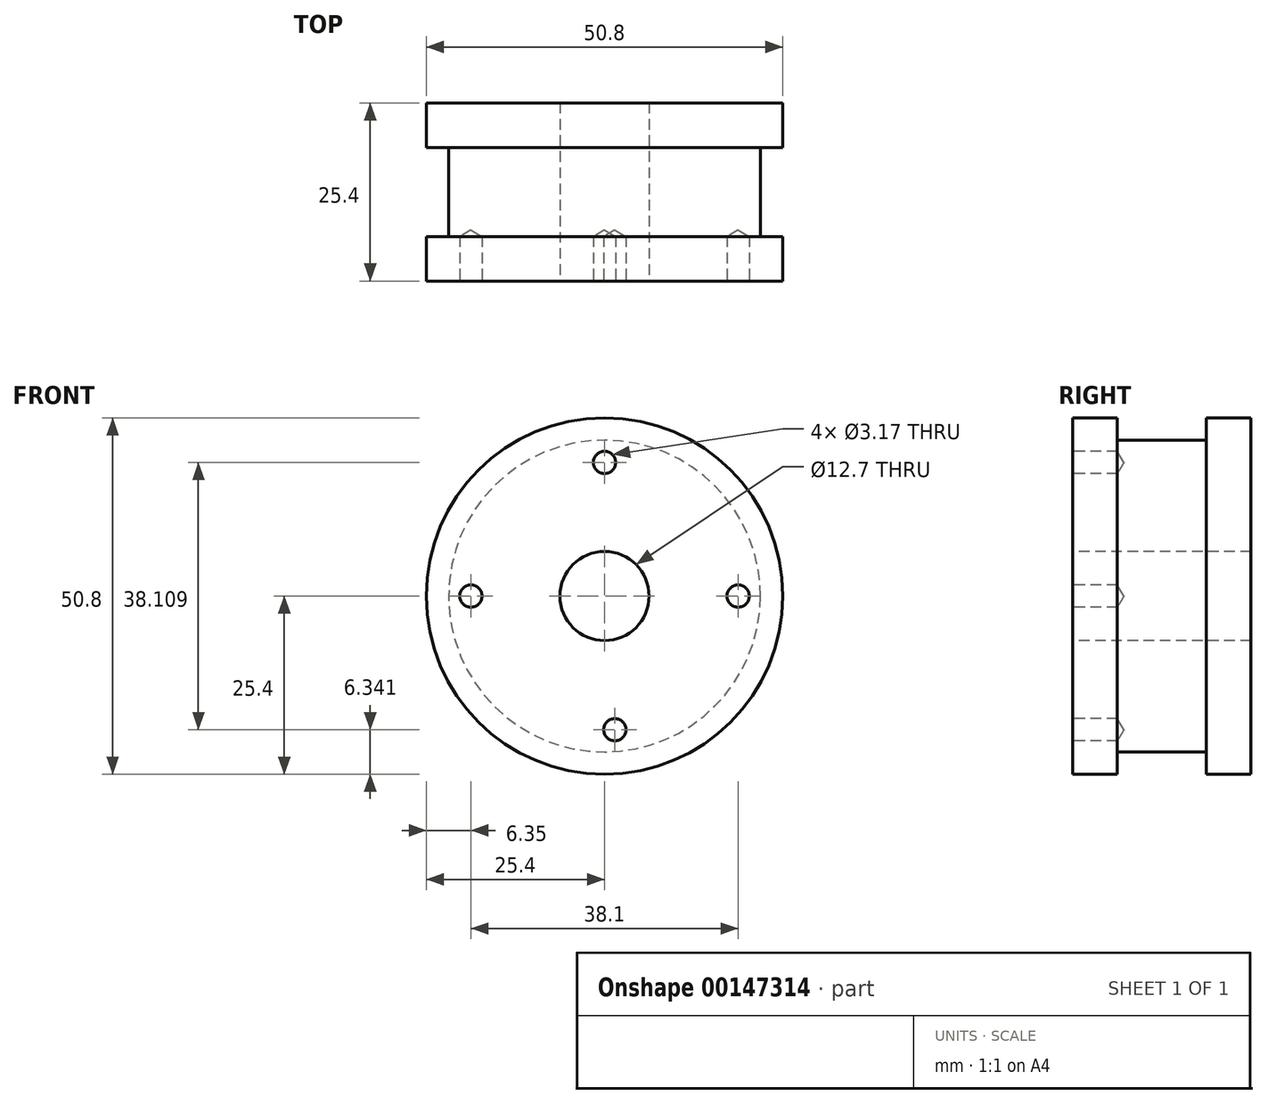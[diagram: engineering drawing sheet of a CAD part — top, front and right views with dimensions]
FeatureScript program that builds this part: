
annotation { "Feature Type Name" : "Feature", "Feature Type Description" : "" }
export const myFeature = defineFeature(function(context is Context, id is Id, definition is map)
    precondition{}
    {
        {
            var Q0;
            Q0=qCreatedBy(makeId("Front.planeOp"),FACE);
            var sketch = newSketch(context, id + "F0", { "sketchPlane" : qUnion([Q0])});
            skCircle(sketch, "E0", {"center": v(0, 0) * mm, "radius": 25.4 * mm});
            skSolve(sketch);
        }
        {
            var Q0;
            Q0 = qSketchRegion(id + "F0", true);
            extrude(context, id + "F1", {"entities" : qUnion([Q0]), "depth" : 6.35 * mm});
        }
        {
            var Q0;
            Q0=makeQuery(id+"F1.opExtrude","CAP_FACE",FACE,{"disambiguationData":[OSD([sQuery(id+"F0.wireOp",EDGE,"E0")])],"isStart":false});
            var sketch = newSketch(context, id + "F2", { "sketchPlane" : qUnion([Q0])});
            skCircle(sketch, "E1", {"center": v(0, 0) * mm, "radius": 22.23 * mm});
            skSolve(sketch);
        }
        {
            var Q0;
            Q0 = qSketchRegion(id + "F2", true);
            extrude(context, id + "F3", {"entities" : qUnion([Q0]), "operationType" : NewBodyOperationType.ADD, "depth" : 12.7 * mm});
        }
        {
            var Q0;
            Q0=makeQuery(id+"F3.opExtrude","CAP_FACE",FACE,{"disambiguationData":[OSD([sQuery(id+"F2.wireOp",EDGE,"E1")])],"isStart":false});
            var sketch = newSketch(context, id + "F4", { "sketchPlane" : qUnion([Q0])});
            skCircle(sketch, "E2", {"center": v(0, 0) * mm, "radius": 25.4 * mm});
            skSolve(sketch);
        }
        {
            var Q0;
            Q0 = qSketchRegion(id + "F4", true);
            extrude(context, id + "F5", {"entities" : qUnion([Q0]), "operationType" : NewBodyOperationType.ADD, "depth" : 6.35 * mm});
        }
        {
            var Q0;
            Q0=makeQuery(id+"F5.opExtrude","CAP_FACE",FACE,{"disambiguationData":[OSD([sQuery(id+"F4.wireOp",EDGE,"E2")])],"isStart":false});
            var sketch = newSketch(context, id + "F6", { "sketchPlane" : qUnion([Q0])});
            skCircle(sketch, "E3", {"center": v(0, -20.64) * mm, "radius": 1.59 * mm});
            skCircle(sketch, "E4", {"center": v(20.64, 0) * mm, "radius": 1.59 * mm});
            skCircle(sketch, "E5", {"center": v(0, 20.64) * mm, "radius": 1.59 * mm});
            skCircle(sketch, "E6", {"center": v(-20.64, 0) * mm, "radius": 1.59 * mm});
            skCircle(sketch, "E7", {"center": v(0, 0) * mm, "radius": 6.35 * mm});
            skSolve(sketch);
        }
        {
            var Q0;
            Q0 = qSketchRegion(id + "F6", true);
            extrude(context, id + "F7", {"entities" : qUnion([Q0]), "operationType" : NewBodyOperationType.REMOVE, "endBound" : BoundingType.THROUGH_ALL, "depth" : 25.4 * mm});
        }
        {
            var Q0;
            Q0=makeQuery(id+"F5.opExtrude","CAP_FACE",FACE,{"disambiguationData":[OSD([sQuery(id+"F4.wireOp",EDGE,"E2")])],"isStart":false});
            var sketch = newSketch(context, id + "F8", { "sketchPlane" : qUnion([Q0])});
            skPoint(sketch, "E8", {"position": v(0, 0) * mm});
            skSolve(sketch);
        }
        {
            var Q0;
            Q0=sQuery(id+"F8.wireOp",VERTEX,"E8");
            var Q1;
            Q1=makeQuery(id+"F1.opExtrude","SWEPT_BODY",BODY,{"disambiguationData":[OSD([sQuery(id+"F0.wireOp",EDGE,"E0")])]});
            hole(context, id + "F9", {"style" : HoleStyle.SIMPLE, "endStyle" : HoleEndStyle.THROUGH, "holeDiameter" : 12.7 * mm, "locations" : qUnion([Q0]), "scope" : qUnion([Q1]), "isTappedThrough" : true});
        }
        {
            var Q0;
            Q0=makeQuery(id+"F5.opExtrude","CAP_FACE",FACE,{"disambiguationData":[OSD([sQuery(id+"F4.wireOp",EDGE,"E2")])],"isStart":false});
            var sketch = newSketch(context, id + "F10", { "sketchPlane" : qUnion([Q0])});
            skPoint(sketch, "E9", {"position": v(19.05, 0) * mm});
            skSolve(sketch);
        }
        {
            var Q0;
            Q0=sQuery(id+"F10.wireOp",VERTEX,"E9");
            var Q1;
            Q1=makeQuery(id+"F1.opExtrude","SWEPT_BODY",BODY,{"disambiguationData":[OSD([sQuery(id+"F0.wireOp",EDGE,"E0")])]});
            hole(context, id + "F11", {"style" : HoleStyle.SIMPLE, "endStyle" : HoleEndStyle.BLIND, "holeDiameter" : 3.17 * mm, "holeDepth" : 6.35 * mm, "locations" : qUnion([Q0]), "scope" : qUnion([Q1])});
        }
        {
            var Q0;
            Q0=makeQuery(id+"F5.opExtrude","CAP_FACE",FACE,{"disambiguationData":[OSD([sQuery(id+"F4.wireOp",EDGE,"E2")])],"isStart":false});
            var sketch = newSketch(context, id + "F12", { "sketchPlane" : qUnion([Q0])});
            skPoint(sketch, "E10", {"position": v(0, 19.05) * mm});
            skSolve(sketch);
        }
        {
            var Q0;
            Q0=sQuery(id+"F12.wireOp",VERTEX,"E10");
            var Q1;
            Q1=makeQuery(id+"F1.opExtrude","SWEPT_BODY",BODY,{"disambiguationData":[OSD([sQuery(id+"F0.wireOp",EDGE,"E0")])]});
            hole(context, id + "F13", {"style" : HoleStyle.SIMPLE, "endStyle" : HoleEndStyle.BLIND, "holeDiameter" : 3.17 * mm, "holeDepth" : 6.35 * mm, "locations" : qUnion([Q0]), "scope" : qUnion([Q1])});
        }
        {
            var Q0;
            Q0=makeQuery(id+"F5.opExtrude","CAP_FACE",FACE,{"disambiguationData":[OSD([sQuery(id+"F4.wireOp",EDGE,"E2")])],"isStart":false});
            var sketch = newSketch(context, id + "F14", { "sketchPlane" : qUnion([Q0])});
            skPoint(sketch, "E11", {"position": v(-19.05, 0) * mm});
            skPoint(sketch, "E12", {"position": v(0, -19.05) * mm});
            skSolve(sketch);
        }
        {
            var Q0;
            Q0=sQuery(id+"F14.wireOp",VERTEX,"E11");
            var Q1;
            Q1=makeQuery(id+"F1.opExtrude","SWEPT_BODY",BODY,{"disambiguationData":[OSD([sQuery(id+"F0.wireOp",EDGE,"E0")])]});
            hole(context, id + "F15", {"style" : HoleStyle.SIMPLE, "endStyle" : HoleEndStyle.BLIND, "holeDiameter" : 3.17 * mm, "holeDepth" : 6.35 * mm, "locations" : qUnion([Q0]), "scope" : qUnion([Q1])});
        }
        {
            var Q0;
            Q0=makeQuery(id+"F5.opExtrude","CAP_FACE",FACE,{"disambiguationData":[OSD([sQuery(id+"F4.wireOp",EDGE,"E2")])],"isStart":false});
            var sketch = newSketch(context, id + "F16", { "sketchPlane" : qUnion([Q0])});
            skPoint(sketch, "E13", {"position": v(1.47, -19.06) * mm});
            skSolve(sketch);
        }
        {
            var Q0;
            Q0=sQuery(id+"F16.wireOp",VERTEX,"E13");
            var Q1;
            Q1=makeQuery(id+"F1.opExtrude","SWEPT_BODY",BODY,{"disambiguationData":[OSD([sQuery(id+"F0.wireOp",EDGE,"E0")])]});
            hole(context, id + "F17", {"style" : HoleStyle.SIMPLE, "endStyle" : HoleEndStyle.BLIND, "holeDiameter" : 3.17 * mm, "holeDepth" : 6.35 * mm, "locations" : qUnion([Q0]), "scope" : qUnion([Q1])});
        }
    });
